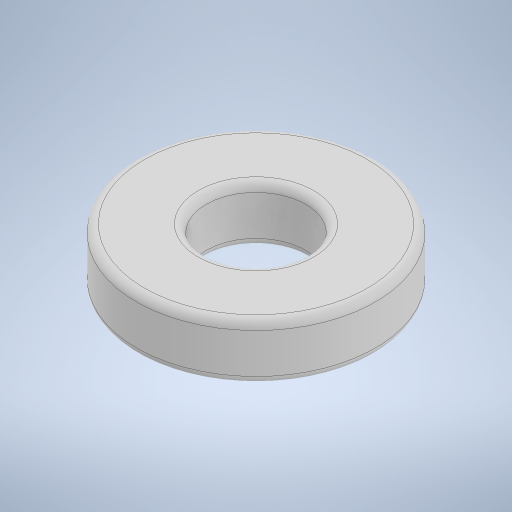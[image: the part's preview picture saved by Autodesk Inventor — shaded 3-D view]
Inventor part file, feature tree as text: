
AUTODESK INVENTOR PART (.ipt)
format: ipt  version: 2023 (Build 270158000, 158)  size: 249,856 bytes
history: native  units: mm
features: fillet x2, extrude x1, sketch x1
ambient origin geometry x8: Origin, YZ Plane, XZ Plane, XY Plane, X Axis, Y Axis, Z Axis, Center Point
bodies: Solid1 (feature_tree)
feature tree (4):
  extrude  "Extrusion1"  Depth=1.0mm
  fillet  "Fillet1"  Radius=7.0mm
  fillet  "Fillet2"  Radius=1.0mm
  sketch  "Sketch1"  dims[d0=12.5mm d1=30.0mm d2=7.0mm d3=0.0mm d4=1.0mm d5=1.0mm]
